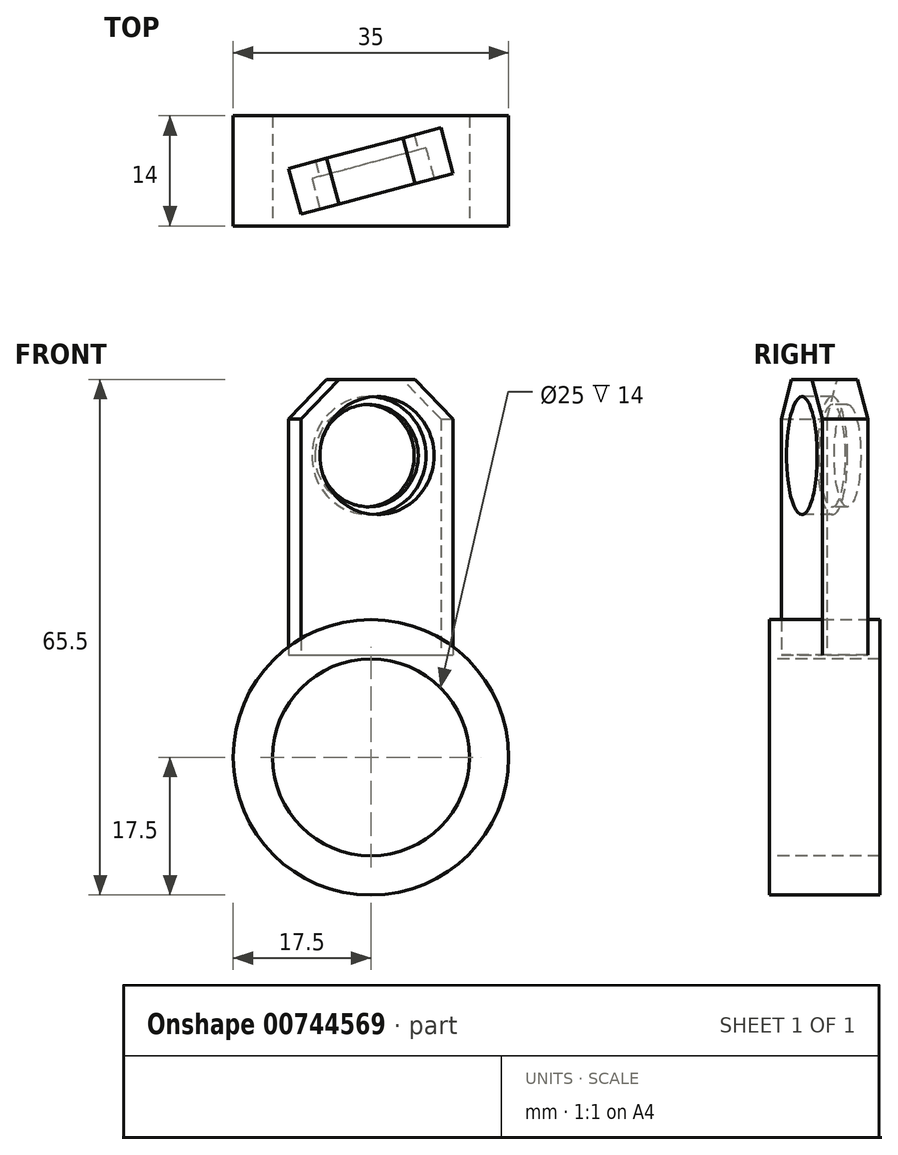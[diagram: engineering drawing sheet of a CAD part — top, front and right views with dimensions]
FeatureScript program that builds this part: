
annotation { "Feature Type Name" : "Feature", "Feature Type Description" : "" }
export const myFeature = defineFeature(function(context is Context, id is Id, definition is map)
    precondition{}
    {
        {
            var Q0;
            Q0=qCreatedBy(makeId("Front.planeOp"),FACE);
            var sketch = newSketch(context, id + "F0", { "sketchPlane" : qUnion([Q0])});
            skCircle(sketch, "E0", {"center": v(0, 0) * mm, "radius": 17.5 * mm});
            skSolve(sketch);
        }
        {
            var Q0;
            Q0 = qSketchRegion(id + "F0", true);
            extrude(context, id + "F1", {"entities" : qUnion([Q0]), "endBound" : BoundingType.SYMMETRIC, "depth" : 14 * mm, "offsetDistance" : 25 * mm});
        }
        {
            var Q0;
            Q0=makeQuery(id+"F1.opExtrude","CAP_FACE",FACE,{"disambiguationData":[OSD([sQuery(id+"F0.wireOp",EDGE,"E0")])],"isStart":false});
            cPlane(context, id + "F2", {"entities" : qUnion([Q0]), "cplaneType" : CPlaneType.OFFSET, "offset" : 0 * mm, "width" : 150 * mm, "height" : 150 * mm});
        }
        {
            var Q0;
            Q0=qCreatedBy(id+"F2.planeOp",FACE);
            var sketch = newSketch(context, id + "F3", { "sketchPlane" : qUnion([Q0])});
            skCircle(sketch, "E1", {"center": v(0, 0) * mm, "radius": 12.5 * mm});
            skSolve(sketch);
        }
        {
            var Q0;
            Q0 = qSketchRegion(id + "F3", true);
            extrude(context, id + "F4", {"entities" : qUnion([Q0]), "operationType" : NewBodyOperationType.REMOVE, "endBound" : BoundingType.THROUGH_ALL, "oppositeDirection" : true, "depth" : 12 * mm, "offsetDistance" : 25 * mm});
        }
        {
            var Q0;
            Q0=qCreatedBy(makeId("Top.planeOp"),FACE);
            cPlane(context, id + "F5", {"entities" : qUnion([Q0]), "cplaneType" : CPlaneType.OFFSET, "offset" : 13 * mm, "width" : 150 * mm, "height" : 150 * mm});
        }
        {
            var Q0;
            Q0=qCreatedBy(id+"F5.planeOp",FACE);
            var sketch = newSketch(context, id + "F6", { "sketchPlane" : qUnion([Q0])});
            skLineSegment(sketch, "E2.top", {"start": v(-8.88, -5.49) * mm, "end": v(10.44, -0.3) * mm});
            skLineSegment(sketch, "E2.left", {"start": v(-10.44, 0.3) * mm, "end": v(-9.66, -2.59) * mm});
            skLineSegment(sketch, "E2.right", {"start": v(8.88, 5.49) * mm, "end": v(9.66, 2.59) * mm});
            skLineSegment(sketch, "E3", {"start": v(-9.66, -2.59) * mm, "end": v(-8.88, -5.49) * mm});
            skLineSegment(sketch, "E4", {"start": v(9.66, 2.59) * mm, "end": v(10.44, -0.3) * mm});
            skPoint(sketch, "E5.orphan", {"position": v(-6.06, -7.7) * mm});
            skPoint(sketch, "E6.end.orphan", {"position": v(7.94, -7.7) * mm});
            skPoint(sketch, "E6.start.orphan", {"position": v(0.94, -7.7) * mm});
            skLineSegment(sketch, "E7", {"start": v(-9.66, -2.59) * mm, "end": v(0, 0) * mm});
            skLineSegment(sketch, "E8", {"start": v(0, 0) * mm, "end": v(9.66, 2.59) * mm});
            skLineSegment(sketch, "E9", {"start": v(-10.44, 0.3) * mm, "end": v(8.88, 5.49) * mm});
            skSolve(sketch);
        }
        {
            var Q0;
            Q0=makeQuery(id+"F6.imprint","IMPRINT",FACE,{"disambiguationData":[TD([[makeQuery(id+"F6.imprint","IMPRINT",EDGE,{"derivedFrom":sQuery(id+"F6.wireOp",EDGE,"E2.left")}),1.0]])]});
            var Q1;
            Q1=makeQuery(id+"F6.imprint","IMPRINT",FACE,{"disambiguationData":[TD([[makeQuery(id+"F6.imprint","IMPRINT",EDGE,{"derivedFrom":sQuery(id+"F6.wireOp",EDGE,"E2.top")}),1.0]])]});
            extrude(context, id + "F7", {"entities" : qUnion([Q0, Q1]), "depth" : 35 * mm, "offsetDistance" : 25 * mm});
        }
        {
            var Q0;
            Q0=qCreatedBy(makeId("Top.planeOp"),FACE);
            var sketch = newSketch(context, id + "F8", { "sketchPlane" : qUnion([Q0])});
            skLineSegment(sketch, "E10", {"start": v(0, -41.26) * mm, "end": v(0, 42.33) * mm});
            skSolve(sketch);
        }
        {
            var Q0;
            Q0=makeQuery(id+"F7.opExtrude","SWEPT_FACE",FACE,{"disambiguationData":[OSD([sQuery(id+"F6.wireOp",EDGE,"E2.top")])]});
            cPlane(context, id + "F9", {"entities" : qUnion([Q0]), "cplaneType" : CPlaneType.OFFSET, "offset" : 0 * mm, "width" : 150 * mm, "height" : 150 * mm});
        }
        {
            var Q0;
            Q0=qCreatedBy(id+"F9.planeOp",FACE);
            var sketch = newSketch(context, id + "F10", { "sketchPlane" : qUnion([Q0])});
            skCircle(sketch, "E11", {"center": v(0, 38.33) * mm, "radius": 7.5 * mm});
            skSolve(sketch);
        }
        {
            var Q0;
            Q0 = qSketchRegion(id + "F10", true);
            extrude(context, id + "F11", {"entities" : qUnion([Q0]), "operationType" : NewBodyOperationType.REMOVE, "oppositeDirection" : true, "depth" : 4 * mm, "offsetDistance" : 25 * mm});
        }
        {
            var Q0;
            Q0=makeQuery(id+"F11.boolean.opBoolean","COPY",FACE,{"derivedFrom":makeQuery(id+"F11.opExtrude","CAP_FACE",FACE,{"disambiguationData":[OSD([sQuery(id+"F10.wireOp",EDGE,"E11")])],"isStart":false})});
            var sketch = newSketch(context, id + "F12", { "sketchPlane" : qUnion([Q0])});
            skCircle(sketch, "E12", {"center": v(0, 38.33) * mm, "radius": 6.5 * mm});
            skSolve(sketch);
        }
        {
            var Q0;
            Q0 = qSketchRegion(id + "F12", true);
            extrude(context, id + "F13", {"entities" : qUnion([Q0]), "operationType" : NewBodyOperationType.REMOVE, "endBound" : BoundingType.THROUGH_ALL, "oppositeDirection" : true, "depth" : 25 * mm, "offsetDistance" : 25 * mm});
        }
        {
            var Q0;
            Q0=makeQuery(id+"F7.opExtrude","CAP_EDGE",EDGE,{"disambiguationData":[OSD([sQuery(id+"F6.wireOp",EDGE,"E2.left"),sQuery(id+"F6.wireOp",EDGE,"E3")])],"isStart":false});
            var Q1;
            Q1=makeQuery(id+"F7.opExtrude","CAP_EDGE",EDGE,{"disambiguationData":[OSD([sQuery(id+"F6.wireOp",EDGE,"E2.right"),sQuery(id+"F6.wireOp",EDGE,"E4")])],"isStart":false});
            var Q2;
            Q2=makeQuery(id+"FlYnf6fdo2lQ6ES_1.2.F7.opExtrude","CAP_EDGE",EDGE,{"disambiguationData":[OSD([sQuery(id+"F6.wireOp",EDGE,"E2.left"),sQuery(id+"F6.wireOp",EDGE,"E3")])],"isStart":false});
            var Q3;
            Q3=makeQuery(id+"FlYnf6fdo2lQ6ES_1.2.F7.opExtrude","CAP_EDGE",EDGE,{"disambiguationData":[OSD([sQuery(id+"F6.wireOp",EDGE,"E2.right"),sQuery(id+"F6.wireOp",EDGE,"E4")])],"isStart":false});
            var Q4;
            Q4=makeQuery(id+"FlYnf6fdo2lQ6ES_1.1.F7.opExtrude","CAP_EDGE",EDGE,{"disambiguationData":[OSD([sQuery(id+"F6.wireOp",EDGE,"E2.right"),sQuery(id+"F6.wireOp",EDGE,"E4")])],"isStart":false});
            var Q5;
            Q5=makeQuery(id+"FlYnf6fdo2lQ6ES_1.1.F7.opExtrude","CAP_EDGE",EDGE,{"disambiguationData":[OSD([sQuery(id+"F6.wireOp",EDGE,"E2.left"),sQuery(id+"F6.wireOp",EDGE,"E3")])],"isStart":false});
            chamfer(context, id + "F14", {"entities" : qUnion([Q0, Q1, Q2, Q3, Q4, Q5]), "width" : 5 * mm, "tangentPropagation" : true});
        }
    });
